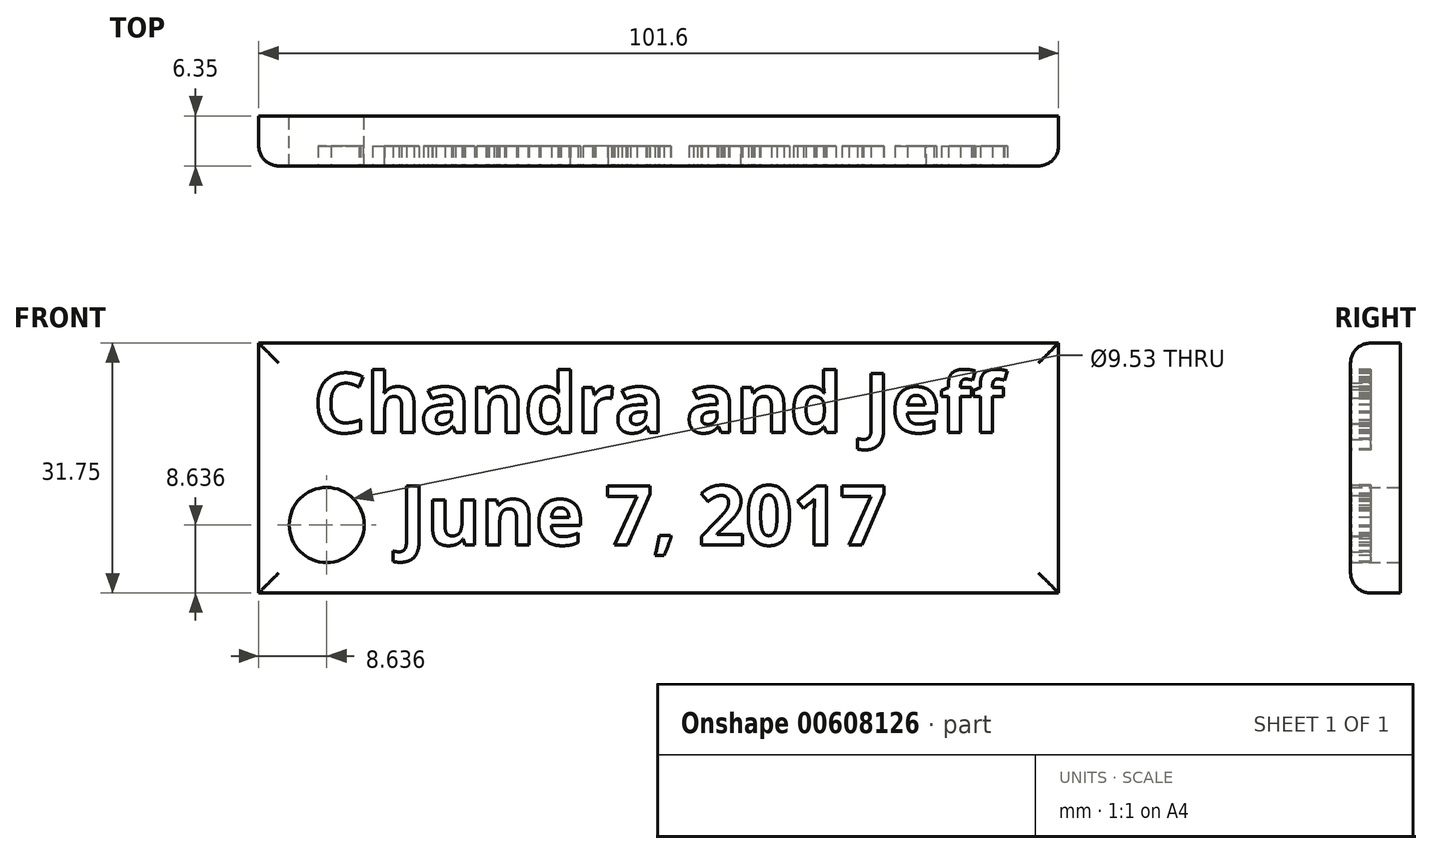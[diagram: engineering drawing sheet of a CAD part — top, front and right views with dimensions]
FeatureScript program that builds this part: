
annotation { "Feature Type Name" : "Feature", "Feature Type Description" : "" }
export const myFeature = defineFeature(function(context is Context, id is Id, definition is map)
    precondition{}
    {
        {
            var Q0;
            Q0=qCreatedBy(makeId("Front.planeOp"),FACE);
            var sketch = newSketch(context, id + "F0", { "sketchPlane" : qUnion([Q0])});
            skLineSegment(sketch, "E0.bottom", {"start": v(0, 0) * mm, "end": v(101.6, 0) * mm});
            skLineSegment(sketch, "E0.top", {"start": v(0, 31.75) * mm, "end": v(101.6, 31.75) * mm});
            skLineSegment(sketch, "E0.left", {"start": v(0, 0) * mm, "end": v(0, 31.75) * mm});
            skLineSegment(sketch, "E0.right", {"start": v(101.6, 0) * mm, "end": v(101.6, 31.75) * mm});
            skCircle(sketch, "E1", {"center": v(8.64, 8.64) * mm, "radius": 4.76 * mm});
            skSolve(sketch);
        }
        {
            var Q0;
            Q0=makeQuery(id+"F0.imprint","IMPRINT",FACE,{"disambiguationData":[TD([[makeQuery(id+"F0.imprint","IMPRINT",EDGE,{"derivedFrom":sQuery(id+"F0.wireOp",EDGE,"E0.bottom")}),1.0]])]});
            extrude(context, id + "F1", {"entities" : qUnion([Q0]), "depth" : 6.35 * mm, "offsetDistance" : 25.4 * mm});
        }
        {
            var Q0;
            Q0=makeQuery(id+"F1.opExtrude","CAP_FACE",FACE,{"disambiguationData":[OSD([sQuery(id+"F0.wireOp",EDGE,"E0.bottom"),sQuery(id+"F0.wireOp",EDGE,"E0.top"),sQuery(id+"F0.wireOp",EDGE,"E0.left"),sQuery(id+"F0.wireOp",EDGE,"E0.right")])],"isStart":false});
            var sketch = newSketch(context, id + "F2", { "sketchPlane" : qUnion([Q0])});
            skText(sketch, "E2", { "text": "Chandra and Jeff\n    June 7, 2017", "fontName": "OpenSans-Bold.ttf"});
            const initialGuessF2  = {"E2": [0.00692, 0.02038, 1, 0, 0.00756]};
            skSetInitialGuess(sketch, initialGuessF2);
            skSolve(sketch);
        }
        {
            var Q0;
            Q0 = qSketchRegion(id + "F2", true);
            extrude(context, id + "F3", {"entities" : qUnion([Q0]), "operationType" : NewBodyOperationType.REMOVE, "oppositeDirection" : true, "depth" : 2.54 * mm, "offsetDistance" : 25.4 * mm});
        }
        {
            var Q0;
            Q0=makeQuery(id+"F1.opExtrude","CAP_EDGE",EDGE,{"disambiguationData":[OSD([sQuery(id+"F0.wireOp",EDGE,"E0.top")])],"isStart":false});
            var Q1;
            Q1=makeQuery(id+"F1.opExtrude","CAP_EDGE",EDGE,{"disambiguationData":[OSD([sQuery(id+"F0.wireOp",EDGE,"E0.left")])],"isStart":false});
            var Q2;
            Q2=makeQuery(id+"F1.opExtrude","CAP_EDGE",EDGE,{"disambiguationData":[OSD([sQuery(id+"F0.wireOp",EDGE,"E0.right")])],"isStart":false});
            var Q3;
            Q3=makeQuery(id+"F1.opExtrude","CAP_EDGE",EDGE,{"disambiguationData":[OSD([sQuery(id+"F0.wireOp",EDGE,"E0.bottom")])],"isStart":false});
            fillet(context, id + "F4", {"entities" : qUnion([Q0, Q1, Q2, Q3]), "radius" : 2.54 * mm, "tangentPropagation" : true, "allowEdgeOverflow" : false});
        }
    });
